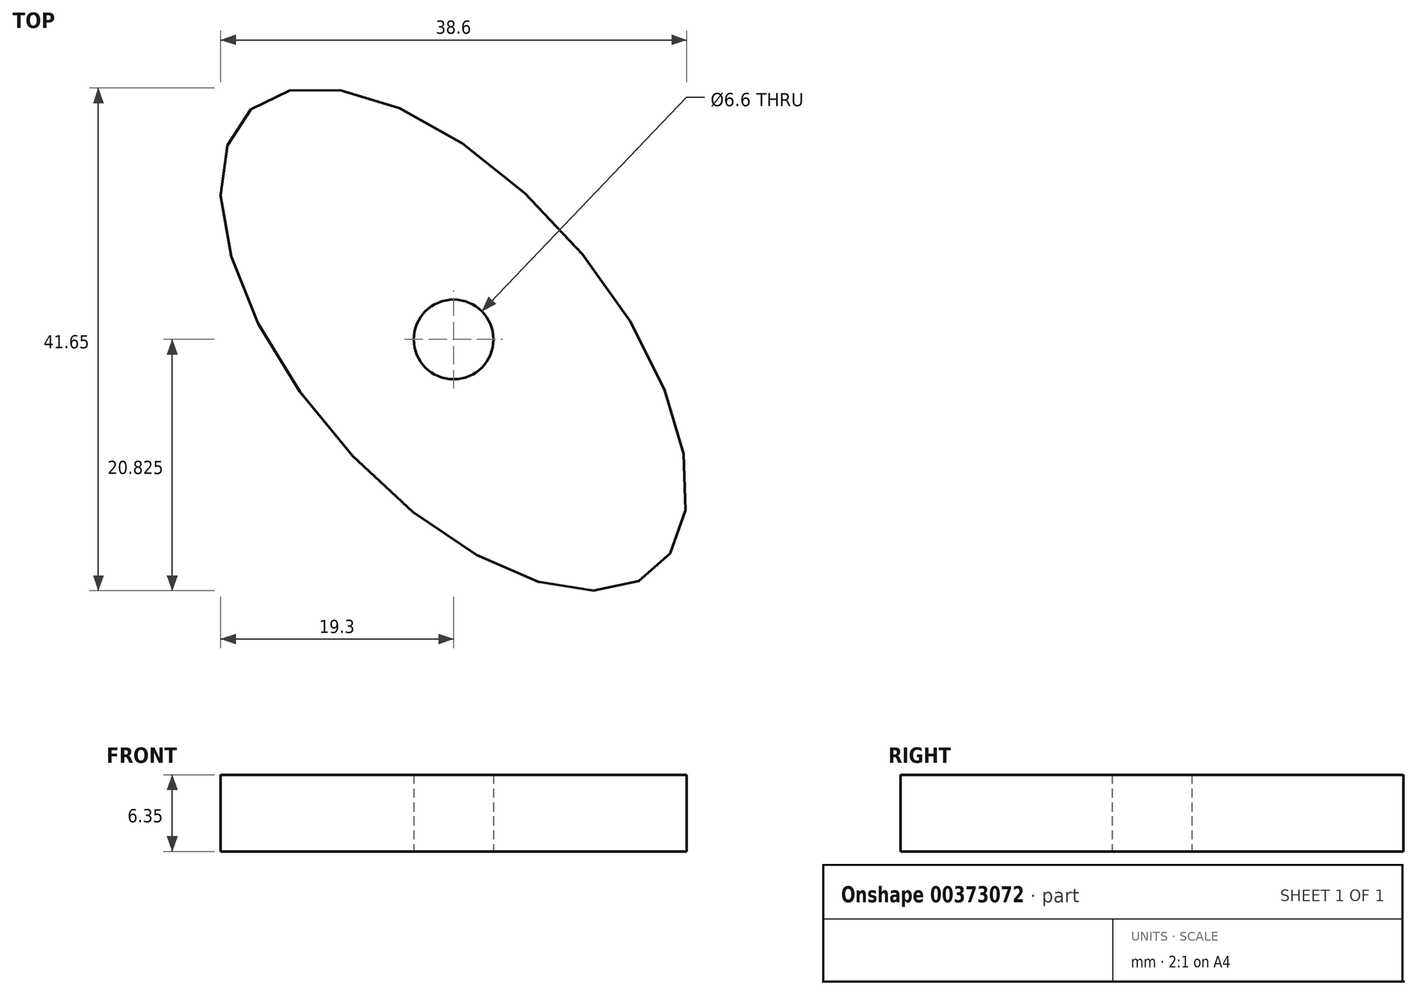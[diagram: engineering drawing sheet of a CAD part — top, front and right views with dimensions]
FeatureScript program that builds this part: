
annotation { "Feature Type Name" : "Feature", "Feature Type Description" : "" }
export const myFeature = defineFeature(function(context is Context, id is Id, definition is map)
    precondition{}
    {
        {
            var Q0;
            Q0=qCreatedBy(makeId("Top.planeOp"),FACE);
            var sketch = newSketch(context, id + "F0", { "sketchPlane" : qUnion([Q0])});
            skEllipse(sketch, "E0", {"center": v(0, -1.86) * mm, "majorRadius": 25.4 * mm, "minorRadius": 12.7 * mm, "majorAxis": v(-0.66, 0.75)});
            skCircle(sketch, "E1", {"center": v(0, -1.86) * mm, "radius": 3.3 * mm});
            skSolve(sketch);
        }
        {
            var Q0;
            Q0 = qSketchRegion(id + "F0", true);
            extrude(context, id + "F1", {"entities" : qUnion([Q0]), "depth" : 6.35 * mm});
        }
    });
